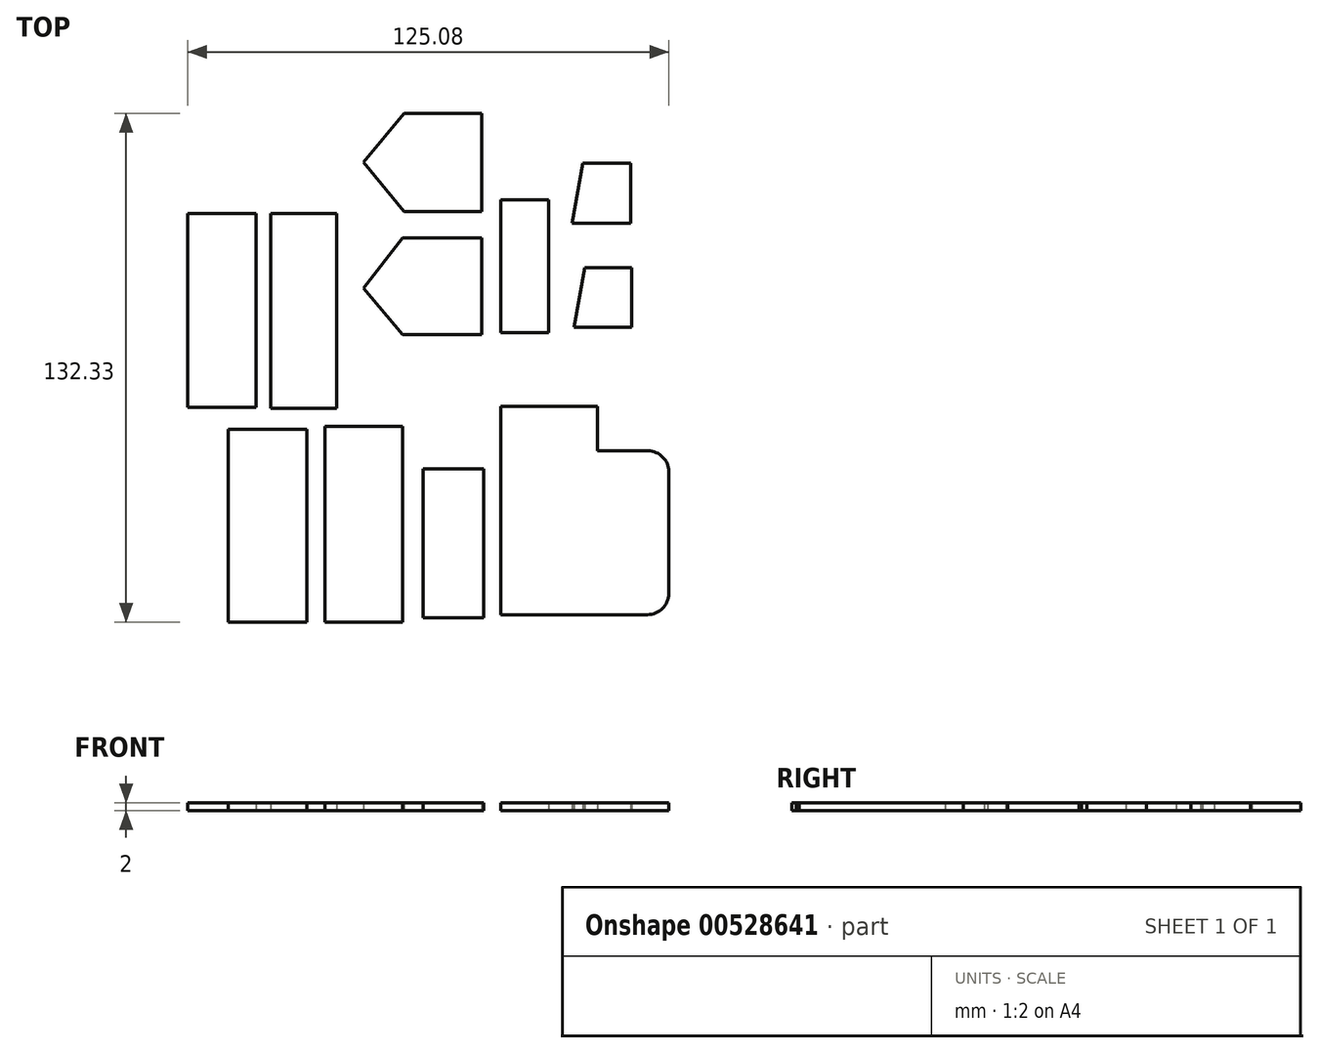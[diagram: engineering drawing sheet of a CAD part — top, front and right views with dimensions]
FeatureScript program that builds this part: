
annotation { "Feature Type Name" : "Feature", "Feature Type Description" : "" }
export const myFeature = defineFeature(function(context is Context, id is Id, definition is map)
    precondition{}
    {
        {
            var Q0;
            Q0=qCreatedBy(makeId("Top.planeOp"),FACE);
            var sketch = newSketch(context, id + "F0", { "sketchPlane" : qUnion([Q0])});
            skLineSegment(sketch, "E0.bottom", {"start": v(-61.74, -71.15) * mm, "end": v(-41.25, -71.15) * mm});
            skLineSegment(sketch, "E0.top", {"start": v(-61.74, -21.04) * mm, "end": v(-41.25, -21.04) * mm});
            skLineSegment(sketch, "E0.left", {"start": v(-61.74, -71.15) * mm, "end": v(-61.74, -21.04) * mm});
            skLineSegment(sketch, "E0.right", {"start": v(-41.25, -71.15) * mm, "end": v(-41.25, -21.04) * mm});
            skLineSegment(sketch, "E1.bottom", {"start": v(-36.54, -71.15) * mm, "end": v(-16.33, -71.15) * mm});
            skLineSegment(sketch, "E1.top", {"start": v(-36.54, -20.21) * mm, "end": v(-16.33, -20.21) * mm});
            skLineSegment(sketch, "E1.left", {"start": v(-36.54, -71.15) * mm, "end": v(-36.54, -20.21) * mm});
            skLineSegment(sketch, "E1.right", {"start": v(-16.33, -71.15) * mm, "end": v(-16.33, -20.21) * mm});
            skSolve(sketch);
        }
        {
            var Q0;
            Q0 = qSketchRegion(id + "F0", true);
            extrude(context, id + "F1", {"entities" : qUnion([Q0]), "depth" : 2 * mm, "offsetDistance" : 25 * mm});
        }
        {
            var Q0;
            Q0=qCreatedBy(makeId("Top.planeOp"),FACE);
            var sketch = newSketch(context, id + "F2", { "sketchPlane" : qUnion([Q0])});
            skLineSegment(sketch, "E2.bottom", {"start": v(-72.26, -15.23) * mm, "end": v(-54.54, -15.23) * mm});
            skLineSegment(sketch, "E2.top", {"start": v(-72.26, 35.16) * mm, "end": v(-54.54, 35.16) * mm});
            skLineSegment(sketch, "E2.left", {"start": v(-72.26, -15.23) * mm, "end": v(-72.26, 35.16) * mm});
            skLineSegment(sketch, "E2.right", {"start": v(-54.54, -15.23) * mm, "end": v(-54.54, 35.16) * mm});
            skLineSegment(sketch, "E3.bottom", {"start": v(-50.66, -15.5) * mm, "end": v(-33.5, -15.5) * mm});
            skLineSegment(sketch, "E3.top", {"start": v(-50.66, 35.16) * mm, "end": v(-33.5, 35.16) * mm});
            skLineSegment(sketch, "E3.left", {"start": v(-50.66, -15.5) * mm, "end": v(-50.66, 35.16) * mm});
            skLineSegment(sketch, "E3.right", {"start": v(-33.5, -15.5) * mm, "end": v(-33.5, 35.16) * mm});
            skSolve(sketch);
        }
        {
            var Q0;
            Q0 = qSketchRegion(id + "F2", true);
            extrude(context, id + "F3", {"entities" : qUnion([Q0]), "depth" : 2 * mm, "offsetDistance" : 25 * mm});
        }
        {
            var Q0;
            Q0=qCreatedBy(makeId("Top.planeOp"),FACE);
            var sketch = newSketch(context, id + "F4", { "sketchPlane" : qUnion([Q0])});
            skLineSegment(sketch, "E4.bottom", {"start": v(-16.33, 3.6) * mm, "end": v(4.15, 3.6) * mm});
            skLineSegment(sketch, "E4.top", {"start": v(-16.33, 28.8) * mm, "end": v(4.15, 28.8) * mm});
            skLineSegment(sketch, "E4.left", {"start": v(-16.33, 3.6) * mm, "end": v(-16.33, 28.8) * mm});
            skLineSegment(sketch, "E4.right", {"start": v(4.15, 3.6) * mm, "end": v(4.15, 28.8) * mm});
            skLineSegment(sketch, "E5", {"start": v(-16.33, 3.6) * mm, "end": v(-26.58, 15.78) * mm});
            skLineSegment(sketch, "E6", {"start": v(-26.58, 15.78) * mm, "end": v(-16.33, 28.8) * mm});
            skLineSegment(sketch, "E7.bottom", {"start": v(-16.06, 35.71) * mm, "end": v(4.15, 35.71) * mm});
            skLineSegment(sketch, "E7.top", {"start": v(-16.06, 61.18) * mm, "end": v(4.15, 61.18) * mm});
            skLineSegment(sketch, "E7.left", {"start": v(-16.06, 35.71) * mm, "end": v(-16.06, 61.18) * mm});
            skLineSegment(sketch, "E7.right", {"start": v(4.15, 35.71) * mm, "end": v(4.15, 61.18) * mm});
            skLineSegment(sketch, "E8", {"start": v(-16.06, 35.71) * mm, "end": v(-26.58, 48.45) * mm});
            skLineSegment(sketch, "E9", {"start": v(-26.58, 48.45) * mm, "end": v(-16.06, 61.18) * mm});
            skSolve(sketch);
        }
        {
            var Q0;
            Q0 = qSketchRegion(id + "F4", true);
            extrude(context, id + "F5", {"entities" : qUnion([Q0]), "depth" : 2 * mm, "offsetDistance" : 25 * mm});
        }
        {
            var Q0;
            Q0=qCreatedBy(makeId("Top.planeOp"),FACE);
            var sketch = newSketch(context, id + "F6", { "sketchPlane" : qUnion([Q0])});
            skLineSegment(sketch, "E10.bottom", {"start": v(-11.07, -70.04) * mm, "end": v(4.7, -70.04) * mm});
            skLineSegment(sketch, "E10.top", {"start": v(-11.07, -31.28) * mm, "end": v(4.7, -31.28) * mm});
            skLineSegment(sketch, "E10.left", {"start": v(-11.07, -70.04) * mm, "end": v(-11.07, -31.28) * mm});
            skLineSegment(sketch, "E10.right", {"start": v(4.7, -70.04) * mm, "end": v(4.7, -31.28) * mm});
            skSolve(sketch);
        }
        {
            var Q0;
            Q0 = qSketchRegion(id + "F6", true);
            extrude(context, id + "F7", {"entities" : qUnion([Q0]), "depth" : 2 * mm, "offsetDistance" : 25 * mm});
        }
        {
            var Q0;
            Q0=qCreatedBy(makeId("Top.planeOp"),FACE);
            var sketch = newSketch(context, id + "F8", { "sketchPlane" : qUnion([Q0])});
            skLineSegment(sketch, "E11.bottom", {"start": v(9.14, 4.15) * mm, "end": v(21.6, 4.15) * mm});
            skLineSegment(sketch, "E11.top", {"start": v(9.14, 38.76) * mm, "end": v(21.6, 38.76) * mm});
            skLineSegment(sketch, "E11.left", {"start": v(9.14, 4.15) * mm, "end": v(9.14, 38.76) * mm});
            skLineSegment(sketch, "E11.right", {"start": v(21.6, 4.15) * mm, "end": v(21.6, 38.76) * mm});
            skSolve(sketch);
        }
        {
            var Q0;
            Q0 = qSketchRegion(id + "F8", true);
            extrude(context, id + "F9", {"entities" : qUnion([Q0]), "depth" : 2 * mm, "offsetDistance" : 25 * mm});
        }
        {
            var Q0;
            Q0=qCreatedBy(makeId("Top.planeOp"),FACE);
            var sketch = newSketch(context, id + "F10", { "sketchPlane" : qUnion([Q0])});
            skLineSegment(sketch, "E12.bottom", {"start": v(9.14, -69.21) * mm, "end": v(34.33, -69.21) * mm});
            skLineSegment(sketch, "E12.top", {"start": v(9.14, -14.96) * mm, "end": v(34.33, -14.96) * mm});
            skLineSegment(sketch, "E12.left", {"start": v(9.14, -69.21) * mm, "end": v(9.14, -14.96) * mm});
            skLineSegment(sketch, "E12.right", {"start": v(34.33, -69.21) * mm, "end": v(34.33, -14.96) * mm});
            skLineSegment(sketch, "E13.bottom", {"start": v(34.33, -69.21) * mm, "end": v(47.29, -69.21) * mm});
            skLineSegment(sketch, "E13.top", {"start": v(34.33, -26.6) * mm, "end": v(47.43, -26.6) * mm});
            skLineSegment(sketch, "E13.left", {"start": v(34.33, -69.21) * mm, "end": v(34.33, -26.6) * mm});
            skLineSegment(sketch, "E13.right", {"start": v(52.82, -63.68) * mm, "end": v(52.82, -31.99) * mm});
            skPoint(sketch, "E14.visualSharp", {"position": v(52.82, -26.6) * mm});
            skArc(sketch, "E14.filletArc", {"start": v(52.82, -31.99) * mm, "mid": v(51.24, -28.18) * mm, "end": v(47.43, -26.6) * mm});
            skPoint(sketch, "E15.visualSharp", {"position": v(52.82, -69.21) * mm});
            skArc(sketch, "E15.filletArc", {"start": v(47.29, -69.21) * mm, "mid": v(51.2, -67.6) * mm, "end": v(52.82, -63.68) * mm});
            skSolve(sketch);
        }
        {
            var Q0;
            Q0 = qSketchRegion(id + "F10", true);
            extrude(context, id + "F11", {"entities" : qUnion([Q0]), "depth" : 2 * mm, "offsetDistance" : 25 * mm});
        }
        {
            var Q0;
            Q0=qCreatedBy(makeId("Top.planeOp"),FACE);
            var sketch = newSketch(context, id + "F12", { "sketchPlane" : qUnion([Q0])});
            skLineSegment(sketch, "E16.bottom", {"start": v(31, 5.54) * mm, "end": v(43.19, 5.54) * mm});
            skLineSegment(sketch, "E16.top", {"start": v(31, 21.04) * mm, "end": v(43.19, 21.04) * mm});
            skLineSegment(sketch, "E16.left", {"start": v(31, 5.54) * mm, "end": v(31, 21.04) * mm});
            skLineSegment(sketch, "E16.right", {"start": v(43.19, 5.54) * mm, "end": v(43.19, 21.04) * mm});
            skLineSegment(sketch, "E17", {"start": v(31, 5.54) * mm, "end": v(28.24, 5.54) * mm});
            skLineSegment(sketch, "E18", {"start": v(28.24, 5.54) * mm, "end": v(31, 21.04) * mm});
            skLineSegment(sketch, "E19.bottom", {"start": v(30.45, 32.67) * mm, "end": v(42.91, 32.67) * mm});
            skLineSegment(sketch, "E19.top", {"start": v(30.45, 48.17) * mm, "end": v(42.91, 48.17) * mm});
            skLineSegment(sketch, "E19.left", {"start": v(30.45, 32.67) * mm, "end": v(30.45, 48.17) * mm});
            skLineSegment(sketch, "E19.right", {"start": v(42.91, 32.67) * mm, "end": v(42.91, 48.17) * mm});
            skLineSegment(sketch, "E20", {"start": v(30.45, 32.67) * mm, "end": v(27.69, 32.67) * mm});
            skLineSegment(sketch, "E21", {"start": v(27.69, 32.67) * mm, "end": v(30.45, 48.17) * mm});
            skSolve(sketch);
        }
        {
            var Q0;
            Q0 = qSketchRegion(id + "F12", true);
            extrude(context, id + "F13", {"entities" : qUnion([Q0]), "depth" : 2 * mm, "offsetDistance" : 25 * mm});
        }
    });
